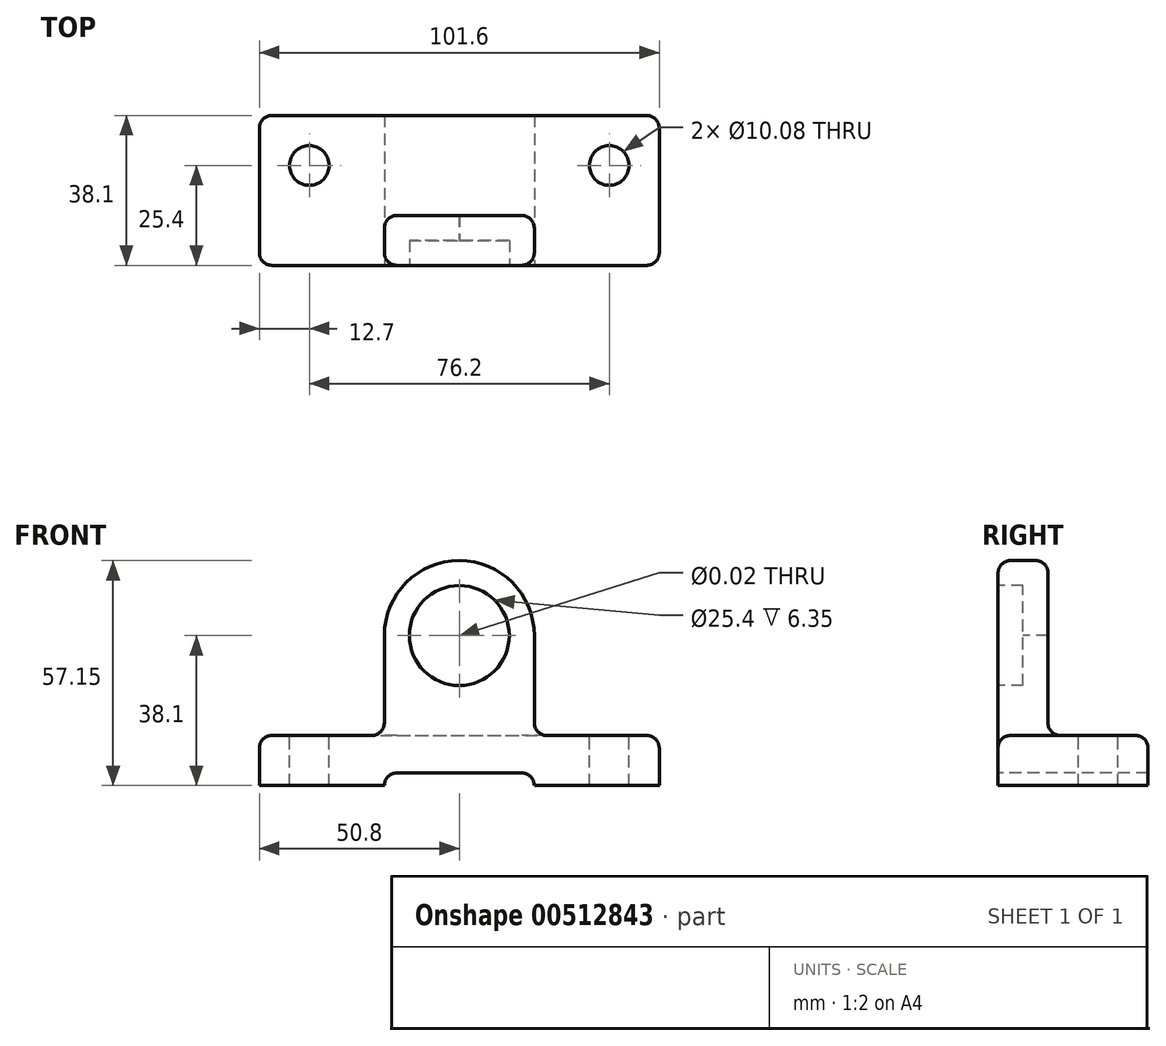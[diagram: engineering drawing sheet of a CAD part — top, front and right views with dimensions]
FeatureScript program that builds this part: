
annotation { "Feature Type Name" : "Feature", "Feature Type Description" : "" }
export const myFeature = defineFeature(function(context is Context, id is Id, definition is map)
    precondition{}
    {
        {
            var Q0;
            Q0=qCreatedBy(makeId("Top.planeOp"),FACE);
            var sketch = newSketch(context, id + "F0", { "sketchPlane" : qUnion([Q0])});
            skLineSegment(sketch, "E0.bottom", {"start": v(0, 0) * mm, "end": v(101.6, 0) * mm});
            skLineSegment(sketch, "E0.top", {"start": v(0, 38.1) * mm, "end": v(101.6, 38.1) * mm});
            skLineSegment(sketch, "E0.left", {"start": v(0, 0) * mm, "end": v(0, 38.1) * mm});
            skLineSegment(sketch, "E0.right", {"start": v(101.6, 0) * mm, "end": v(101.6, 38.1) * mm});
            skSolve(sketch);
        }
        {
            var Q0;
            Q0=makeQuery(id+"F0.imprint","IMPRINT",FACE,{"disambiguationData":[TD([[makeQuery(id+"F0.imprint","IMPRINT",EDGE,{"derivedFrom":sQuery(id+"F0.wireOp",EDGE,"E0.bottom")}),1.0]])]});
            extrude(context, id + "F1", {"entities" : qUnion([Q0]), "depth" : 12.7 * mm, "offsetDistance" : 25.4 * mm});
        }
        {
            var Q0;
            Q0=qCreatedBy(makeId("Front.planeOp"),FACE);
            var sketch = newSketch(context, id + "F2", { "sketchPlane" : qUnion([Q0])});
            skLineSegment(sketch, "E1", {"start": v(31.75, 0) * mm, "end": v(31.75, 38.1) * mm});
            skArc(sketch, "E2", {"start": v(69.85, 38.1) * mm, "mid": v(50.8, 57.15) * mm, "end": v(31.75, 38.1) * mm});
            skLineSegment(sketch, "E3", {"start": v(69.85, 38.1) * mm, "end": v(69.85, 0) * mm});
            skLineSegment(sketch, "E4", {"start": v(69.85, 0) * mm, "end": v(31.75, 0) * mm});
            skSolve(sketch);
        }
        {
            var Q0;
            Q0=makeQuery(id+"F2.imprint","IMPRINT",FACE,{"disambiguationData":[TD([[makeQuery(id+"F2.imprint","IMPRINT",EDGE,{"derivedFrom":sQuery(id+"F2.wireOp",EDGE,"E1")}),-1.0]])]});
            extrude(context, id + "F3", {"entities" : qUnion([Q0]), "operationType" : NewBodyOperationType.ADD, "oppositeDirection" : true, "depth" : 12.7 * mm, "offsetDistance" : 25.4 * mm});
        }
        {
            var Q0;
            Q0=makeQuery(id+"F3.boolean.opBoolean","MERGE",FACE,{"derivedFrom":[makeQuery(id+"F1.opExtrude","SWEPT_FACE",FACE,{"disambiguationData":[OSD([sQuery(id+"F0.wireOp",EDGE,"E0.bottom")])]}),makeQuery(id+"F3.opExtrude","CAP_FACE",FACE,{"disambiguationData":[OSD([sQuery(id+"F2.wireOp",EDGE,"E1"),sQuery(id+"F2.wireOp",EDGE,"E2"),sQuery(id+"F2.wireOp",EDGE,"E3"),sQuery(id+"F2.wireOp",EDGE,"E4")])],"isStart":true})]});
            var sketch = newSketch(context, id + "F4", { "sketchPlane" : qUnion([Q0])});
            skPoint(sketch, "E5", {"position": v(50.8, 38.1) * mm});
            skSolve(sketch);
        }
        {
            var Q0;
            Q0=sQuery(id+"F4.wireOp",VERTEX,"E5");
            var Q1;
            Q1=makeQuery(id+"F1.opExtrude","SWEPT_BODY",BODY,{"disambiguationData":[OSD([sQuery(id+"F0.wireOp",EDGE,"E0.bottom"),sQuery(id+"F0.wireOp",EDGE,"E0.top"),sQuery(id+"F0.wireOp",EDGE,"E0.left"),sQuery(id+"F0.wireOp",EDGE,"E0.right")])]});
            hole(context, id + "F5", {"style" : HoleStyle.C_BORE, "endStyle" : HoleEndStyle.THROUGH, "standardTappedOrClearance" : lookupTablePath({ "standard" : "ANSI", "size" : "15/32 (0.47)", "type" : "Drilled" }), "standardBlindInLast" : lookupTablePath({ "standard" : "ANSI", "size" : "15/32", "type" : "Drilled" }), "holeDiameter" : 15 / 812.8 * mm, "cBoreDiameter" : 25.4 * mm, "cBoreDepth" : 6.35 * mm, "isTappedThrough" : true, "tappedDepth" : 12.7 * mm, "tapClearance" : 3, "locations" : qUnion([Q0]), "scope" : qUnion([Q1])});
        }
        {
            var Q0;
            Q0=makeQuery(id+"F3.boolean.opBoolean","MERGE",FACE,{"derivedFrom":[makeQuery(id+"F1.opExtrude","SWEPT_FACE",FACE,{"disambiguationData":[OSD([sQuery(id+"F0.wireOp",EDGE,"E0.bottom")])]}),makeQuery(id+"F3.opExtrude","CAP_FACE",FACE,{"disambiguationData":[OSD([sQuery(id+"F2.wireOp",EDGE,"E1"),sQuery(id+"F2.wireOp",EDGE,"E2"),sQuery(id+"F2.wireOp",EDGE,"E3"),sQuery(id+"F2.wireOp",EDGE,"E4")])],"isStart":true})]});
            var sketch = newSketch(context, id + "F6", { "sketchPlane" : qUnion([Q0])});
            skLineSegment(sketch, "E6", {"start": v(31.75, 0) * mm, "end": v(69.85, 0) * mm});
            skLineSegment(sketch, "E7", {"start": v(69.85, 0) * mm, "end": v(69.85, 3.18) * mm});
            skLineSegment(sketch, "E8", {"start": v(69.85, 3.18) * mm, "end": v(31.75, 3.17) * mm});
            skLineSegment(sketch, "E9", {"start": v(31.75, 3.17) * mm, "end": v(31.75, 0) * mm});
            skSolve(sketch);
        }
        {
            var Q0;
            Q0=makeQuery(id+"F6.imprint","IMPRINT",FACE,{"disambiguationData":[TD([[makeQuery(id+"F6.imprint","IMPRINT",EDGE,{"derivedFrom":sQuery(id+"F6.wireOp",EDGE,"E6")}),1.0]])]});
            extrude(context, id + "F7", {"entities" : qUnion([Q0]), "operationType" : NewBodyOperationType.REMOVE, "endBound" : BoundingType.THROUGH_ALL, "oppositeDirection" : true, "depth" : 25.4 * mm, "offsetDistance" : 25.4 * mm});
        }
        {
            var Q0;
            Q0=makeQuery(id+"F1.opExtrude","CAP_FACE",FACE,{"disambiguationData":[OSD([sQuery(id+"F0.wireOp",EDGE,"E0.bottom"),sQuery(id+"F0.wireOp",EDGE,"E0.top"),sQuery(id+"F0.wireOp",EDGE,"E0.left"),sQuery(id+"F0.wireOp",EDGE,"E0.right")])],"isStart":false});
            var sketch = newSketch(context, id + "F8", { "sketchPlane" : qUnion([Q0])});
            skPoint(sketch, "E10", {"position": v(12.7, 25.4) * mm});
            skPoint(sketch, "E11", {"position": v(88.9, 25.4) * mm});
            skSolve(sketch);
        }
        {
            var Q0;
            Q0=sQuery(id+"F8.wireOp",VERTEX,"E10");
            var Q1;
            Q1=sQuery(id+"F8.wireOp",VERTEX,"E11");
            var Q2;
            Q2=makeQuery(id+"F1.opExtrude","SWEPT_BODY",BODY,{"disambiguationData":[OSD([sQuery(id+"F0.wireOp",EDGE,"E0.bottom"),sQuery(id+"F0.wireOp",EDGE,"E0.top"),sQuery(id+"F0.wireOp",EDGE,"E0.left"),sQuery(id+"F0.wireOp",EDGE,"E0.right")])]});
            hole(context, id + "F9", {"style" : HoleStyle.SIMPLE, "endStyle" : HoleEndStyle.THROUGH, "standardTappedOrClearance" : lookupTablePath({ "standard" : "ANSI", "fit" : "Normal (ASME)", "size" : "3/8", "type" : "Clearance" }), "standardBlindInLast" : lookupTablePath({ "fit" : "Free", "standard" : "ANSI", "size" : "3/8", "type" : "Clearance" }), "holeDiameter" : 10.08 * mm, "isTappedThrough" : true, "tappedDepth" : 12.7 * mm, "tapClearance" : 3, "locations" : qUnion([Q0, Q1]), "scope" : qUnion([Q2])});
        }
        {
            var Q0;
            Q0=makeQuery(id+"F1.opExtrude","SWEPT_EDGE",EDGE,{"disambiguationData":[OSD([sQuery(id+"F0.wireOp",EDGE,"E0.bottom"),sQuery(id+"F0.wireOp",EDGE,"E0.left")])]});
            var Q1;
            Q1=makeQuery(id+"F1.opExtrude","SWEPT_EDGE",EDGE,{"disambiguationData":[OSD([sQuery(id+"F0.wireOp",EDGE,"E0.top"),sQuery(id+"F0.wireOp",EDGE,"E0.left")])]});
            var Q2;
            Q2=makeQuery(id+"F1.opExtrude","SWEPT_EDGE",EDGE,{"disambiguationData":[OSD([sQuery(id+"F0.wireOp",EDGE,"E0.bottom"),sQuery(id+"F0.wireOp",EDGE,"E0.right")])]});
            var Q3;
            Q3=makeQuery(id+"F1.opExtrude","SWEPT_EDGE",EDGE,{"disambiguationData":[OSD([sQuery(id+"F0.wireOp",EDGE,"E0.top"),sQuery(id+"F0.wireOp",EDGE,"E0.right")])]});
            var Q4;
            Q4=makeQuery(id+"F7.boolean.opBoolean","COPY",EDGE,{"derivedFrom":makeQuery(id+"F7.opExtrude","SWEPT_EDGE",EDGE,{"disambiguationData":[OSD([sQuery(id+"F6.wireOp",EDGE,"E8"),sQuery(id+"F6.wireOp",EDGE,"E9")])]})});
            var Q5;
            Q5=makeQuery(id+"F7.boolean.opBoolean","COPY",EDGE,{"derivedFrom":makeQuery(id+"F7.opExtrude","SWEPT_EDGE",EDGE,{"disambiguationData":[OSD([sQuery(id+"F6.wireOp",EDGE,"E7"),sQuery(id+"F6.wireOp",EDGE,"E8")])]})});
            fillet(context, id + "F10", {"entities" : qUnion([Q0, Q1, Q2, Q3, Q4, Q5]), "radius" : 3.17 * mm, "tangentPropagation" : true, "allowEdgeOverflow" : false});
        }
        {
            var Q0;
            Q0=makeQuery(id+"F1.opExtrude","CAP_EDGE",EDGE,{"disambiguationData":[OSD([sQuery(id+"F0.wireOp",EDGE,"E0.top")])],"isStart":false});
            var Q1;
            Q1=makeQuery(id+"F1.opExtrude","CAP_EDGE",EDGE,{"disambiguationData":[OSD([sQuery(id+"F0.wireOp",EDGE,"E0.right")])],"isStart":false});
            var Q2;
            {var subQ0=sQuery(id+"F0.wireOp",EDGE,"E0.right");var subQ1=sQuery(id+"F0.wireOp",EDGE,"E0.top");Q2=makeQuery(id+"F10.opFillet","BLEND_EDGE",EDGE,{"blendedFrom":[makeQuery(id+"F1.opExtrude","SWEPT_EDGE",EDGE,{"disambiguationData":[OSD([subQ1,subQ0])]}),makeQuery(id+"F1.opExtrude","CAP_FACE",FACE,{"disambiguationData":[OSD([sQuery(id+"F0.wireOp",EDGE,"E0.bottom"),subQ1,sQuery(id+"F0.wireOp",EDGE,"E0.left"),subQ0])],"isStart":false})],"blendedInto":[makeQuery(id+"F1.opExtrude","CAP_FACE",FACE,{"disambiguationData":[OSD([sQuery(id+"F0.wireOp",EDGE,"E0.bottom"),subQ1,sQuery(id+"F0.wireOp",EDGE,"E0.left"),subQ0])],"isStart":false})]});}
            var Q3;
            {var subQ0=sQuery(id+"F0.wireOp",EDGE,"E0.right");var subQ1=sQuery(id+"F0.wireOp",EDGE,"E0.bottom");Q3=makeQuery(id+"F10.opFillet","BLEND_EDGE",EDGE,{"blendedFrom":[makeQuery(id+"F1.opExtrude","SWEPT_EDGE",EDGE,{"disambiguationData":[OSD([subQ1,subQ0])]}),makeQuery(id+"F1.opExtrude","CAP_FACE",FACE,{"disambiguationData":[OSD([subQ1,sQuery(id+"F0.wireOp",EDGE,"E0.top"),sQuery(id+"F0.wireOp",EDGE,"E0.left"),subQ0])],"isStart":false})],"blendedInto":[makeQuery(id+"F1.opExtrude","CAP_FACE",FACE,{"disambiguationData":[OSD([subQ1,sQuery(id+"F0.wireOp",EDGE,"E0.top"),sQuery(id+"F0.wireOp",EDGE,"E0.left"),subQ0])],"isStart":false})]});}
            var Q4;
            {var subQ1=sQuery(id+"F0.wireOp",EDGE,"E0.right");var subQ2=sQuery(id+"F0.wireOp",EDGE,"E0.bottom");Q4=makeQuery(id+"F3.boolean.opBoolean","SPLIT",EDGE,{"disambiguationData":[TD([makeQuery(id+"F1.opExtrude","SWEPT_FACE",FACE,{"disambiguationData":[OSD([subQ1])]})])],"derivedFrom":makeQuery(id+"F1.opExtrude","CAP_EDGE",EDGE,{"disambiguationData":[OSD([subQ2])],"isStart":false})});}
            var Q5;
            {var subQ0=sQuery(id+"F0.wireOp",EDGE,"E0.left");var subQ1=sQuery(id+"F0.wireOp",EDGE,"E0.top");Q5=makeQuery(id+"F10.opFillet","BLEND_EDGE",EDGE,{"blendedFrom":[makeQuery(id+"F1.opExtrude","SWEPT_EDGE",EDGE,{"disambiguationData":[OSD([subQ1,subQ0])]}),makeQuery(id+"F1.opExtrude","CAP_FACE",FACE,{"disambiguationData":[OSD([sQuery(id+"F0.wireOp",EDGE,"E0.bottom"),subQ1,subQ0,sQuery(id+"F0.wireOp",EDGE,"E0.right")])],"isStart":false})],"blendedInto":[makeQuery(id+"F1.opExtrude","CAP_FACE",FACE,{"disambiguationData":[OSD([sQuery(id+"F0.wireOp",EDGE,"E0.bottom"),subQ1,subQ0,sQuery(id+"F0.wireOp",EDGE,"E0.right")])],"isStart":false})]});}
            var Q6;
            Q6=makeQuery(id+"F1.opExtrude","CAP_EDGE",EDGE,{"disambiguationData":[OSD([sQuery(id+"F0.wireOp",EDGE,"E0.left")])],"isStart":false});
            var Q7;
            {var subQ0=sQuery(id+"F0.wireOp",EDGE,"E0.left");var subQ1=sQuery(id+"F0.wireOp",EDGE,"E0.bottom");Q7=makeQuery(id+"F10.opFillet","BLEND_EDGE",EDGE,{"blendedFrom":[makeQuery(id+"F1.opExtrude","SWEPT_EDGE",EDGE,{"disambiguationData":[OSD([subQ1,subQ0])]}),makeQuery(id+"F1.opExtrude","CAP_FACE",FACE,{"disambiguationData":[OSD([subQ1,sQuery(id+"F0.wireOp",EDGE,"E0.top"),subQ0,sQuery(id+"F0.wireOp",EDGE,"E0.right")])],"isStart":false})],"blendedInto":[makeQuery(id+"F1.opExtrude","CAP_FACE",FACE,{"disambiguationData":[OSD([subQ1,sQuery(id+"F0.wireOp",EDGE,"E0.top"),subQ0,sQuery(id+"F0.wireOp",EDGE,"E0.right")])],"isStart":false})]});}
            var Q8;
            {var subQ1=sQuery(id+"F0.wireOp",EDGE,"E0.left");var subQ2=sQuery(id+"F0.wireOp",EDGE,"E0.bottom");Q8=makeQuery(id+"F3.boolean.opBoolean","SPLIT",EDGE,{"disambiguationData":[TD([makeQuery(id+"F1.opExtrude","SWEPT_FACE",FACE,{"disambiguationData":[OSD([subQ1])]})])],"derivedFrom":makeQuery(id+"F1.opExtrude","CAP_EDGE",EDGE,{"disambiguationData":[OSD([subQ2])],"isStart":false})});}
            var Q9;
            Q9=makeQuery(id+"F3.opExtrude","CAP_EDGE",EDGE,{"disambiguationData":[OSD([sQuery(id+"F2.wireOp",EDGE,"E1")])],"isStart":true});
            var Q10;
            Q10=makeQuery(id+"F3.opExtrude","CAP_EDGE",EDGE,{"disambiguationData":[OSD([sQuery(id+"F2.wireOp",EDGE,"E2")])],"isStart":true});
            var Q11;
            Q11=makeQuery(id+"F3.opExtrude","CAP_EDGE",EDGE,{"disambiguationData":[OSD([sQuery(id+"F2.wireOp",EDGE,"E3")])],"isStart":true});
            var Q12;
            Q12=makeQuery(id+"F3.boolean.opBoolean","INTERSECT",EDGE,{"derivedFrom":[makeQuery(id+"F1.opExtrude","CAP_FACE",FACE,{"disambiguationData":[OSD([sQuery(id+"F0.wireOp",EDGE,"E0.bottom"),sQuery(id+"F0.wireOp",EDGE,"E0.top"),sQuery(id+"F0.wireOp",EDGE,"E0.left"),sQuery(id+"F0.wireOp",EDGE,"E0.right")])],"isStart":false}),makeQuery(id+"F3.opExtrude","SWEPT_FACE",FACE,{"disambiguationData":[OSD([sQuery(id+"F2.wireOp",EDGE,"E3")])]})]});
            var Q13;
            Q13=makeQuery(id+"F3.boolean.opBoolean","INTERSECT",EDGE,{"derivedFrom":[makeQuery(id+"F1.opExtrude","CAP_FACE",FACE,{"disambiguationData":[OSD([sQuery(id+"F0.wireOp",EDGE,"E0.bottom"),sQuery(id+"F0.wireOp",EDGE,"E0.top"),sQuery(id+"F0.wireOp",EDGE,"E0.left"),sQuery(id+"F0.wireOp",EDGE,"E0.right")])],"isStart":false}),makeQuery(id+"F3.opExtrude","SWEPT_FACE",FACE,{"disambiguationData":[OSD([sQuery(id+"F2.wireOp",EDGE,"E1")])]})]});
            var Q14;
            Q14=makeQuery(id+"F3.boolean.opBoolean","INTERSECT",EDGE,{"derivedFrom":[makeQuery(id+"F1.opExtrude","CAP_FACE",FACE,{"disambiguationData":[OSD([sQuery(id+"F0.wireOp",EDGE,"E0.bottom"),sQuery(id+"F0.wireOp",EDGE,"E0.top"),sQuery(id+"F0.wireOp",EDGE,"E0.left"),sQuery(id+"F0.wireOp",EDGE,"E0.right")])],"isStart":false}),makeQuery(id+"F3.opExtrude","CAP_FACE",FACE,{"disambiguationData":[OSD([sQuery(id+"F2.wireOp",EDGE,"E1"),sQuery(id+"F2.wireOp",EDGE,"E2"),sQuery(id+"F2.wireOp",EDGE,"E3"),sQuery(id+"F2.wireOp",EDGE,"E4")])],"isStart":false})]});
            var Q15;
            Q15=makeQuery(id+"F3.opExtrude","CAP_EDGE",EDGE,{"disambiguationData":[OSD([sQuery(id+"F2.wireOp",EDGE,"E1")])],"isStart":false});
            var Q16;
            Q16=makeQuery(id+"F3.opExtrude","CAP_EDGE",EDGE,{"disambiguationData":[OSD([sQuery(id+"F2.wireOp",EDGE,"E2")])],"isStart":false});
            var Q17;
            Q17=makeQuery(id+"F3.opExtrude","CAP_EDGE",EDGE,{"disambiguationData":[OSD([sQuery(id+"F2.wireOp",EDGE,"E3")])],"isStart":false});
            fillet(context, id + "F11", {"entities" : qUnion([Q0, Q1, Q2, Q3, Q4, Q5, Q6, Q7, Q8, Q9, Q10, Q11, Q12, Q13, Q14, Q15, Q16, Q17]), "radius" : 3.17 * mm, "tangentPropagation" : true, "allowEdgeOverflow" : false});
        }
    });
